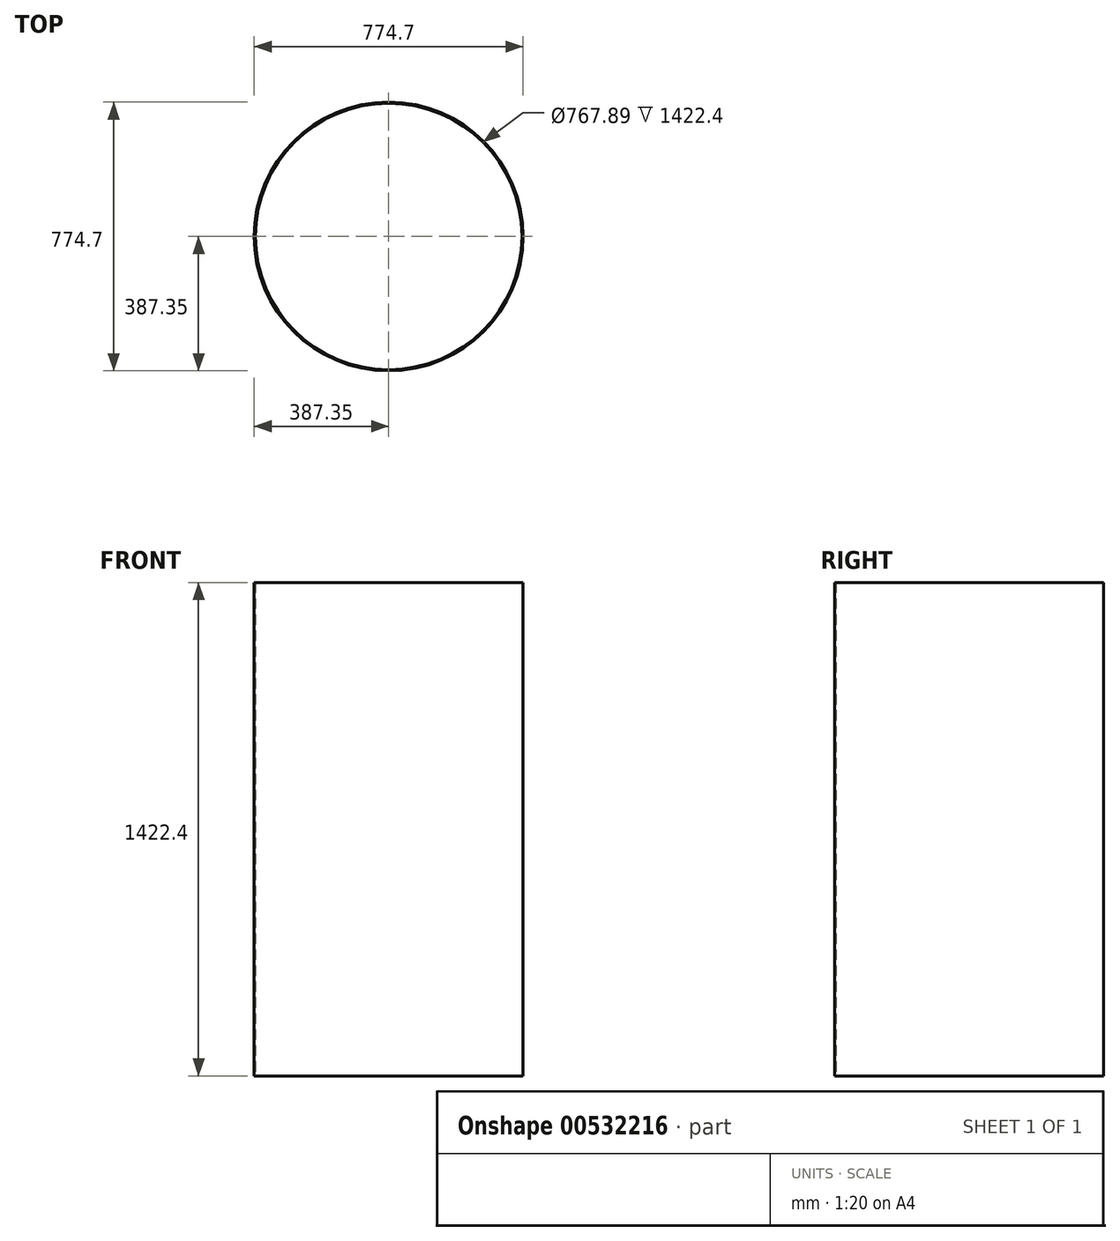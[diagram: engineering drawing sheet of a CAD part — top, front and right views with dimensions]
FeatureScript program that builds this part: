
annotation { "Feature Type Name" : "Feature", "Feature Type Description" : "" }
export const myFeature = defineFeature(function(context is Context, id is Id, definition is map)
    precondition{}
    {
        {
            var Q0;
            Q0=qCreatedBy(makeId("Top.planeOp"),FACE);
            var sketch = newSketch(context, id + "F0", { "sketchPlane" : qUnion([Q0])});
            skCircle(sketch, "E0", {"center": v(0, 0) * mm, "radius": 387.35 * mm});
            skCircle(sketch, "E1", {"center": v(0, 0) * mm, "radius": 383.95 * mm});
            skSolve(sketch);
        }
        {
            var Q0;
            Q0=makeQuery(id+"F0.imprint","IMPRINT",FACE,{"disambiguationData":[TD([[makeQuery(id+"F0.imprint","IMPRINT",EDGE,{"derivedFrom":sQuery(id+"F0.wireOp",EDGE,"E0")}),1.0]])]});
            extrude(context, id + "F1", {"entities" : qUnion([Q0]), "depth" : 1422.4 * mm, "offsetDistance" : 25.4 * mm});
        }
    });
